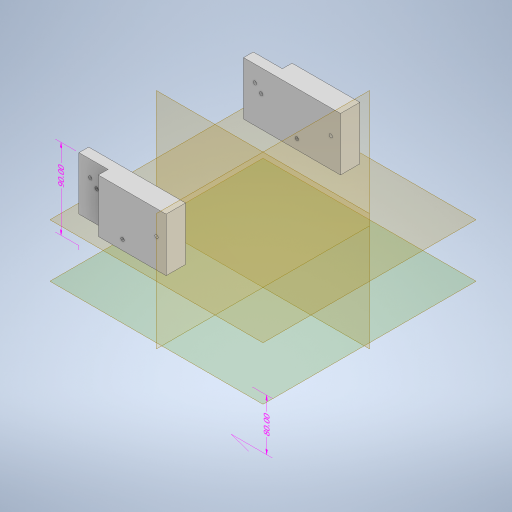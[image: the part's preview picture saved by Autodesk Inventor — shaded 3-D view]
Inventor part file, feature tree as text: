
AUTODESK INVENTOR PART (.ipt)
format: ipt  version: 2023 (Build 270158000, 158)  size: 432,128 bytes
history: native  units: mm
features: sketch x9, extrude x5, other x4, hole x4, plane x4, split x3
ambient origin geometry x8: Origin, YZ Plane, XZ Plane, XY Plane, X Axis, Y Axis, Z Axis, Center Point
bodies: Body1 (feature_tree)
feature tree (29):
  other  "Sólido1"
  other  "Anotaciones"
  extrude  "Extrusión1"  Depth=200.0mm
  hole  "Agujero1"  [1 undecoded]
  extrude  "Extrusión2"  Depth=15.0mm
  extrude  "Extrusión3"  Depth=20.0mm TaperAngle=0.0deg
  extrude  "Extrusión4"  Depth=200.0mm
  extrude  "Extrusión5"  Depth=20.0mm
  hole  "Agujero2"  [1 undecoded]
  plane  "Plano de trabajo1"
  split  "Dividir1"
  plane  "Plano de trabajo2"
  plane  "Plano de trabajo3"
  sketch  "Boceto9"  dims[d37=20.0mm d38=20.0mm]
  plane  "Plano de trabajo4"
  hole  "Agujero3"  [1 undecoded]
  hole  "Agujero4"  [1 undecoded]
  split  "Dividir2"
  split  "Dividir3"
  sketch  "Boceto2"  dims[d7=15.0mm d8=200.0mm]
  sketch  "Boceto3"  dims[d9=10.0mm d10=0.0mm]
  sketch  "Boceto4"  dims[d12=1.75mm d13=1.75mm d14=1.75mm d15=1.75mm d16=10.0mm d17=10.0mm d19=30.0mm]
  sketch  "Boceto5"  dims[d20=3.5mm d21=6.0mm d22=4.0mm d23=2.0mm d24=90.0deg d25=8.0mm d26=20.594885mm d27=15.0mm]
  sketch  "Boceto6"  dims[d28=20.0mm d29=80.0mm d30=0.0mm]
  sketch  "Boceto7"  dims[d31=48.0mm d32=200.0mm]
  sketch  "Boceto8"  dims[d33=110.0mm d34=0.0mm d36=20.0mm]
  sketch  "Boceto10"  dims[d39=90.0mm d40=0.0mm d42=10.0mm d43=30.0mm d44=0.0mm d46=1.75mm d47=1.75mm d48=1.75mm d49=1.75mm d50=10.0mm d51=10.0mm d52=15.0mm d56=3.5mm d57=6.0mm d58=4.0mm d59=2.0mm d60=90.0deg d61=8.0mm d62=20.594885mm d63=10.0mm d65=10.0mm d66=10.0mm d67=31.75mm d70=15.0mm d74=200.0mm d78=20.0mm d82=90.0deg d83=10.0mm d84=30.0mm d85=5.0mm d86=5.0mm d87=5.0mm d88=5.0mm d89=20.0mm d91=30.0mm d92=5.0mm d93=5.0mm d94=3.5mm d95=5.0mm d96=5.0mm d97=5.0mm d98=5.0mm d99=5.0mm d100=20.0mm d101=3.5mm d102=6.0mm d103=4.0mm d104=2.0mm d105=90.0deg d106=8.0mm d107=20.594885mm d108=10.0mm d109=30.0mm d110=5.0mm d111=5.0mm d112=5.0mm d113=5.0mm d114=5.0mm d115=5.0mm d116=3.5mm d117=5.0mm d118=5.0mm d119=5.0mm d120=5.0mm d121=5.0mm d122=30.0mm d123=30.0mm d124=3.5mm d125=6.0mm d126=4.0mm d127=2.0mm d128=90.0deg d129=8.0mm d130=20.594885mm d75=1.454734mm d76=6.982969mm d77=80.0mm d79=4.097996mm d80=1.406125mm d81=90.0mm]
  other  "Cota lineal 2"
  other  "Cota lineal 3"
note: 4 required parameter values undecoded (feature->parameter linkage not recoverable at this tier; creation-order binding heuristic only, values carry confidence <= 0.55)
